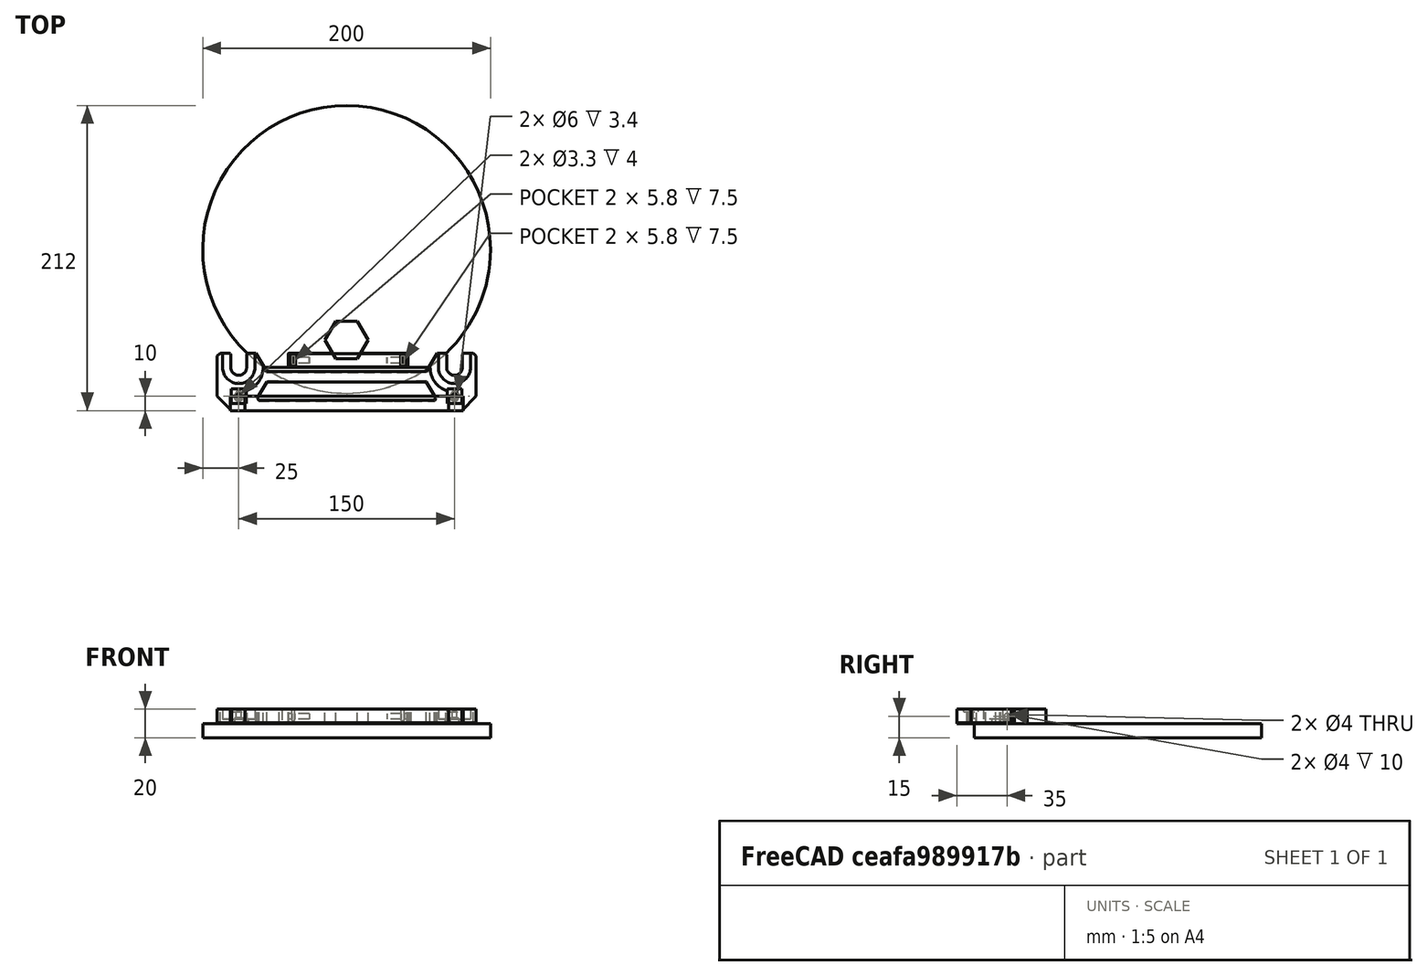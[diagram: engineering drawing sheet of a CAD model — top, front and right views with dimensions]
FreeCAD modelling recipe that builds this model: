
FCSTD DOCUMENT  (FreeCAD 0.18R14555 (Git shallow))
Label: base
License: All rights reserved
LicenseURL: http://en.wikipedia.org/wiki/All_rights_reserved
objects: Part::Box×17, Part::Cut×12, Part::Cylinder×9, Part::MultiFuse×8, Part::Feature×8, Part::Chamfer×6
note: 60 computed .brp shape members not serialized (recipe doc carries the construction recipe); baked Part::Feature solids carry a one-line shape summary decoded from their .brp

FEATURE [Part::Cylinder] Cylinder004
  Angle = 360
  AttacherType = Attacher::AttachEngine3D
  Height = 10
  Placement = pos=(0,82,-10) rot=(0,0,1;0rad)
  Radius = 100
FEATURE [Part::Cylinder] Cylinder
  Angle = 360
  AttacherType = Attacher::AttachEngine3D
  Height = 10
  Placement = pos=(0,0,3) rot=(0,0,1;0rad)
  Radius = 11.2
FEATURE [Part::Cylinder] Cylinder005
  Angle = 360
  AttacherType = Attacher::AttachEngine3D
  Height = 10
  Radius = 5.5
FEATURE [Part::Box] Box  label="Cube"
  AttacherType = Attacher::AttachEngine3D
  Height = 10
  Length = 11
  Placement = pos=(-5.5,0,0) rot=(0,0,1;0rad)
  Width = 20
FEATURE [Part::Box] Box001  label="Cube001"
  AttacherType = Attacher::AttachEngine3D
  Height = 10
  Length = 22.4
  Placement = pos=(-11.2,0,3) rot=(0,0,1;0rad)
  Width = 20
FEATURE [Part::MultiFuse] Fusion
  Placement = pos=(-75,0,0) rot=(0,0,1;0rad)
  Shapes = -> [Box001,Cylinder,Box,Cylinder005]
FEATURE [Part::Feature] Fusion001
  Placement = pos=(75,0,0) rot=(0,0,1;0rad)
  shape: bbox 22.4 x 31.2 x 13 mm, 20 faces (baked)
FEATURE [Part::Box] Box002  label="Cube002"
  AttacherType = Attacher::AttachEngine3D
  Height = 10
  Length = 180
  Placement = pos=(-90,-30,0) rot=(0,0,1;0rad)
  Width = 40
FEATURE [Part::Cut] Cut
  Base = -> Box002
  Tool = -> Fusion
FEATURE [Part::Cylinder] Cylinder006
  Angle = 360
  AttacherType = Attacher::AttachEngine3D
  Height = 10
  Placement = pos=(-75,0,0) rot=(0,0,1;0rad)
  Radius = 17
FEATURE [Part::Cylinder] Cylinder007
  Angle = 360
  AttacherType = Attacher::AttachEngine3D
  Height = 10
  Placement = pos=(75,0,0) rot=(0,0,1;0rad)
  Radius = 17
FEATURE [Part::Box] Box003  label="Cube003"
  AttacherType = Attacher::AttachEngine3D
  Height = 10
  Length = 140
  Placement = pos=(-70,-20,0) rot=(0,0,1;0rad)
  Width = 20
FEATURE [Part::Cut] Cut002
  Base = -> Box003
  Tool = -> Cylinder007
FEATURE [Part::Cut] Cut003
  Base = -> Cut002
  Tool = -> Cylinder006
FEATURE [Part::Chamfer] Chamfer
  Base = -> Cut003
  Edges = 2 edges r=1: [Edge4,Edge16]
FEATURE [Part::Box] Box004  label="Cube004"
  AttacherType = Attacher::AttachEngine3D
  Height = 10
  Length = 10.2
  Placement = pos=(-81,-30,0) rot=(0,0,1;0rad)
  Width = 10
FEATURE [Part::Box] Box005  label="Cube005"
  AttacherType = Attacher::AttachEngine3D
  Height = 10
  Length = 10.2
  Placement = pos=(70.8,-30,0) rot=(0,0,1;0rad)
  Width = 10
FEATURE [Part::Feature] Body001
  Placement = pos=(-48,10,0) rot=(0,0,1;0rad)
  shape: bbox 30 x 25.98 x 10 mm, 8 faces (baked)
FEATURE [Part::Feature] Body002
  Placement = pos=(0,19,0) rot=(0,0,1;0rad)
  shape: bbox 30 x 25.98 x 10 mm, 8 faces (baked)
FEATURE [Part::Feature] Body003
  Placement = pos=(48,10,0) rot=(0,0,1;0rad)
  shape: bbox 30 x 25.98 x 10 mm, 8 faces (baked)
FEATURE [Part::Feature] Body006
  Placement = pos=(-48,-23,0) rot=(0,0,1;0rad)
  shape: bbox 30 x 25.98 x 10 mm, 8 faces (baked)
FEATURE [Part::Feature] Body007
  Placement = pos=(48,-23,0) rot=(0,0,1;0rad)
  shape: bbox 30 x 25.98 x 10 mm, 8 faces (baked)
FEATURE [Part::Box] Box006  label="Cube006"
  AttacherType = Attacher::AttachEngine3D
  Height = 10
  Length = 32
  Placement = pos=(-64,-43,0) rot=(0,0,1;0rad)
  Width = 20
FEATURE [Part::Box] Box007  label="Cube007"
  AttacherType = Attacher::AttachEngine3D
  Height = 10
  Length = 32
  Placement = pos=(32,-43,0) rot=(0,0,1;0rad)
  Width = 20
FEATURE [Part::Box] Box008  label="Cube008"
  AttacherType = Attacher::AttachEngine3D
  Height = 10
  Length = 89
  Placement = pos=(-45,-3,0) rot=(0,0,1;0rad)
  Width = 14
FEATURE [Part::Cut] Cut001
  Base = -> Cut
  Tool = -> Fusion001
FEATURE [Part::Cut] Cut006
  Base = -> Body006
  Tool = -> Box006
FEATURE [Part::Cut] Cut007
  Base = -> Body007
  Tool = -> Box007
FEATURE [Part::MultiFuse] Fusion002
  Shapes = -> [Body001,Body003,Box008]
FEATURE [Part::Cut] Cut008
  Base = -> Cut001
  Tool = -> Fusion002
FEATURE [Part::Box] Box009  label="Cube009"
  AttacherType = Attacher::AttachEngine3D
  Height = 10
  Length = 92
  Placement = pos=(-47,-23,0) rot=(0,0,1;0rad)
  Width = 13
FEATURE [Part::MultiFuse] Fusion003
  Shapes = -> [Cut007,Cut006,Box009]
FEATURE [Part::Cut] Cut009
  Base = -> Cut008
  Tool = -> Fusion003
FEATURE [Part::Chamfer] Chamfer001
  Base = -> Cut009
  Edges = 2 edges r=10: [Edge1,Edge6]
FEATURE [Part::Cylinder] Cylinder008
  Angle = 360
  AttacherType = Attacher::AttachEngine3D
  Height = 4
  Radius = 3
FEATURE [Part::Box] Box010  label="Cube010"
  AttacherType = Attacher::AttachEngine3D
  Height = 0.2
  Length = 10
  Placement = pos=(1.65,-5,0) rot=(0,0,1;0rad)
  Width = 10
FEATURE [Part::Box] Box011  label="Cube011"
  AttacherType = Attacher::AttachEngine3D
  Height = 0.2
  Length = 10
  Placement = pos=(-11.65,-5,0) rot=(0,0,1;0rad)
  Width = 10
FEATURE [Part::Box] Box012  label="Cube012"
  AttacherType = Attacher::AttachEngine3D
  Height = 0.4
  Length = 10
  Placement = pos=(-5,1.65,0) rot=(0,0,1;0rad)
  Width = 10
FEATURE [Part::Box] Box013  label="Cube013"
  AttacherType = Attacher::AttachEngine3D
  Height = 0.4
  Length = 10
  Placement = pos=(-5,-11.65,0) rot=(0,0,1;0rad)
  Width = 10
FEATURE [Part::MultiFuse] Fusion004
  Shapes = -> [Box012,Box011,Box013,Box010]
FEATURE [Part::Cut] Cut010
  Base = -> Cylinder008
  Placement = pos=(0,5e-16,4) rot=(1,0,0;3.14159rad)
  Tool = -> Fusion004
FEATURE [Part::Cylinder] Cylinder009
  Angle = 360
  AttacherType = Attacher::AttachEngine3D
  Height = 15
  Radius = 1.65
FEATURE [Part::MultiFuse] Fusion005
  Placement = pos=(-75,-20,0) rot=(0,0,1;0rad)
  Shapes = -> [Cylinder009,Cut010]
FEATURE [Part::Box] Box014  label="Cube014"
  AttacherType = Attacher::AttachEngine3D
  Height = 10
  Length = 10.2
  Placement = pos=(-80.1,-25.1,8) rot=(0,0,1;0rad)
  Width = 10.2
FEATURE [Part::MultiFuse] Fusion006
  Shapes = -> [Box014,Fusion005]
FEATURE [Part::Feature] Fusion006001  label="Fusion007"
  Placement = pos=(150,0,0) rot=(0,0,1;0rad)
  shape: bbox 10.2 x 10.2 x 18 mm, 26 faces (baked)
FEATURE [Part::MultiFuse] Fusion006002
  Shapes = -> [Fusion006,Fusion006001]
FEATURE [Part::Cut] Cut011
  Base = -> Chamfer001
  Tool = -> Fusion006002
FEATURE [Part::Chamfer] Chamfer002
  Base = -> Cut011
  Edges = 4 edges r=2: [Edge3,Edge91,Edge125,Edge130]
FEATURE [Part::Chamfer] Chamfer003
  Base = -> Chamfer002
  Edges = 4 edges r=1: [Edge91,Edge106,Edge107,Edge120]
FEATURE [Part::Chamfer] Chamfer004
  Base = -> Chamfer003
  Edges = 44 edges r=0.4: [Edge1,Edge2,Edge3,Edge4,Edge5,Edge6,Edge7,Edge8,Edge9,Edge10,Edge11,Edge12,Edge13,Edge14,Edge15,Edge16,Edge17,Edge18,Edge19,Edge20,Edge21,Edge22,Edge23,Edge24,Edge25,Edge26,Edge27,Edge28,Edge29,Edge30,Edge31,Edge32,Edge33,Edge34,Edge35,Edge36,Edge37,Edge38,Edge39,Edge40,Edge41,Edge42,Edge43,Edge44]
FEATURE [Part::Box] Box015  label="Cube015"
  AttacherType = Attacher::AttachEngine3D
  Height = 10
  Length = 83
  Placement = pos=(-40.5,0,0) rot=(0,0,1;0rad)
  Width = 10
FEATURE [Part::Cylinder] Cylinder010
  Angle = 360
  AttacherType = Attacher::AttachEngine3D
  Height = 10
  Placement = pos=(-1.1e-15,0,5) rot=(0,1,0;4.71239rad)
  Radius = 2
FEATURE [Part::Box] Box016  label="Cube016"
  AttacherType = Attacher::AttachEngine3D
  Height = 13.8
  Length = 2
  Placement = pos=(0,-2.9,2.1) rot=(0,0,1;0rad)
  Width = 5.8
FEATURE [Part::Cylinder] Cylinder011
  Angle = 360
  AttacherType = Attacher::AttachEngine3D
  Height = 10
  Placement = pos=(12,0,5) rot=(0,-1,0;1.5708rad)
  Radius = 2
FEATURE [Part::MultiFuse] Fusion006003
  Placement = pos=(-38,5,0) rot=(0,0,1;0rad)
  Shapes = -> [Cylinder010,Box016,Cylinder011]
FEATURE [Part::Feature] Fusion006003001  label="Fusion006004"
  Placement = pos=(38,5,0) rot=(0,0,1;0rad)
  shape: bbox 22 x 5.8 x 13.8 mm, 10 faces (baked)
FEATURE [Part::Cut] Cut012
  Base = -> Box015
  Tool = -> Fusion006003001
FEATURE [Part::Cut] Cut013
  Base = -> Cut012
  Tool = -> Fusion006003
FEATURE [Part::Chamfer] Chamfer005
  Base = -> Cut013
  Edges = 18 edges r=0.4: [Edge1,Edge2,Edge3,Edge4,Edge6,Edge7,Edge8,Edge9,Edge10,Edge11,Edge13,Edge14,Edge15,Edge16,Edge17,Edge19,Edge20,Edge21]
